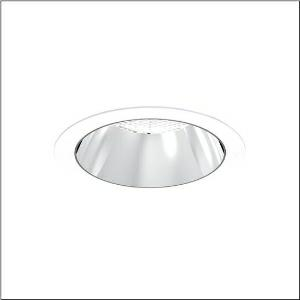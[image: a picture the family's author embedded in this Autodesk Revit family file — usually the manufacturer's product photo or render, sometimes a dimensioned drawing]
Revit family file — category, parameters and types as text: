
# Revit family: lunis_21_xl_51db15ef91c
name_source: partatom
category: Lighting Fixtures
units: mm (PartAtom-declared; Revit-internal decimal feet)

## family parameters
Cut with Voids When Loaded = No
Host = Face
Light Source = No
Part Type = Normal
Room Calculation Point = No
Round Connector Dimension = Use Diameter
Shared = No

## types (1)
- --- (1 x LED, 4110 lm, 25.4 W, 6500K)
    Apparent Load = 25 VA
    CIE Flux Codes = 92 100 100 100 100
    Color Rendering = 80
    Color Temperature = 6500K
    Default Elevation = 1800 mm
    Description = Lunis 21 XL, downlight, light control with lens, of PMMA, anti glare with reflector, of PC, highly specular, light emission: direct distribution, LED rated luminous flux: 2.430lm, light colour: 830/840/865, with terminal, 5-pole, mains connection: 220..240V, AC/DC, 0/50..60Hz, housing, round, of diecast aluminium, traffic white (RAL 9016), diameter: 230mm, clamping range: 1..40mm, protection rating (complete): IP20, protection rating (on room side): IP54, insulation class (complete): insulation class II (safety insulation), certification: CE, impact resistance: IK03, packaging unit: 1 piece
    Height = 0 mm  [stored 0 ft]
    Lamp = 1 x LED
    Lamp Light Flux = 4110 lm
    Lamp Power = 25.4 W
    Lamp count = 1
    Length = 230 mm
    Luminous efficacy = 162 lm/W
    Manufacturer = Siteco
    ModVariant = No
    Model = 51DB15EF91C
    Mounting Place = Ceiling
    Mounting Type = Recessed
    Number of Poles = 1
    OnlyDefault = Yes
    Power Factor = 1
    Product Name = Lunis 21 XL
    Product group = downlight
    ProductGroupID = 401
    Protection Class = Protection class II
    Protection Degree = IP 20
    RLX_Detail_Level = 1
    RLX_Emergency_Light_Flux = 0 lm
    RLX_Emergency_Type = 0
    RLX_Emergency_Type_DB = No
    RlxData = <blob elided: 22209 chars, md5=57378e60>
    Socket = socket
    Standby Power = 0 W
    System Light Flux = 4110 lm
    System Power = 25 W
    Type Comments = individual setting: colour temperature 6500K, luminous flux: 100 % | (ON | ON | OFF | OFF) | 700 mA
    Type Image = l_1291156.jpg
    URL = http://relux.com
    VarID = @adj_036121
    Voltage = 0 V
    Weight = 0.00 kg
    Width = 0 mm  [stored 0 ft]

note: [stored X ft] marks values corroborated as IEEE doubles in the binary element streams (Revit-internal decimal feet)

## geometry (parser evidence)
native form markers: Blend x4, Sweep x9
no freeform markers — native parametric forms only
